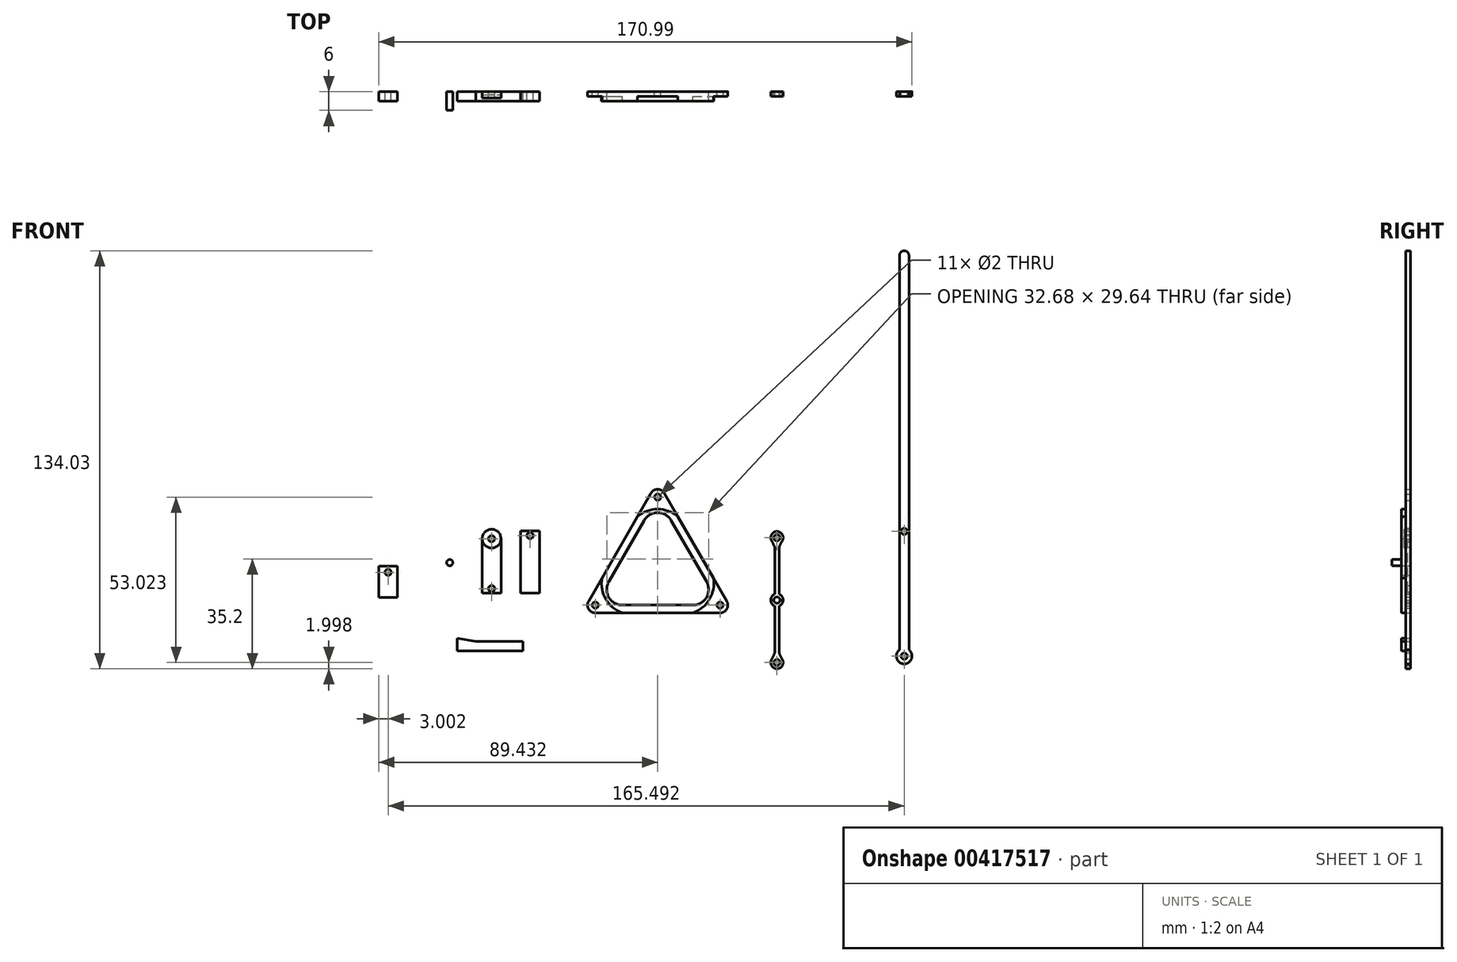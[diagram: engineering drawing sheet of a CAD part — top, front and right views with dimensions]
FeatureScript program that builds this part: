
annotation { "Feature Type Name" : "Feature", "Feature Type Description" : "" }
export const myFeature = defineFeature(function(context is Context, id is Id, definition is map)
    precondition{}
    {
        {
            var Q0;
            Q0=qCreatedBy(makeId("Front.planeOp"),FACE);
            var sketch = newSketch(context, id + "F0", { "sketchPlane" : qUnion([Q0])});
            skLineSegment(sketch, "E0.top", {"start": v(-62.3, 0) * mm, "end": v(-39.63, 0) * mm});
            skLineSegment(sketch, "E1", {"start": v(-55.3, 27.14) * mm, "end": v(-66.64, 7.5) * mm});
            skLineSegment(sketch, "E2", {"start": v(-46.64, 27.14) * mm, "end": v(-35.3, 7.5) * mm});
            skPoint(sketch, "E0.right.start.orphan", {"position": v(-30.97, 34.64) * mm});
            skPoint(sketch, "E0.bottom.start.orphan", {"position": v(-70.97, 34.64) * mm});
            skCircle(sketch, "E3", {"center": v(-50.97, 34.64) * mm, "radius": 2.5 * mm});
            skCircle(sketch, "E4", {"center": v(-70.97, 0) * mm, "radius": 2.5 * mm});
            skCircle(sketch, "E5", {"center": v(-30.97, 0) * mm, "radius": 2.5 * mm});
            skLineSegment(sketch, "E6", {"start": v(-70.97, -2.5) * mm, "end": v(-30.97, -2.5) * mm});
            skLineSegment(sketch, "E7", {"start": v(-28.8, 1.25) * mm, "end": v(-48.8, 35.9) * mm});
            skLineSegment(sketch, "E8", {"start": v(-53.13, 35.9) * mm, "end": v(-73.13, 1.25) * mm});
            skArc(sketch, "E9.filletArc", {"start": v(-66.64, 7.5) * mm, "mid": v(-66.64, 2.5) * mm, "end": v(-62.3, 0) * mm});
            skArc(sketch, "E10.filletArc", {"start": v(-39.63, 0) * mm, "mid": v(-35.3, 2.5) * mm, "end": v(-35.3, 7.5) * mm});
            skArc(sketch, "E11.filletArc", {"start": v(-46.64, 27.14) * mm, "mid": v(-50.97, 29.64) * mm, "end": v(-55.3, 27.14) * mm});
            skArc(sketch, "E12", {"start": v(-44.47, 28.4) * mm, "mid": v(-50.97, 30.79) * mm, "end": v(-57.46, 28.4) * mm});
            skArc(sketch, "E13", {"start": v(-68.8, 8.75) * mm, "mid": v(-67.63, 1.93) * mm, "end": v(-62.3, -2.5) * mm});
            skArc(sketch, "E14", {"start": v(-39.7, -2.5) * mm, "mid": v(-34.33, 1.9) * mm, "end": v(-33.13, 8.75) * mm});
            skCircle(sketch, "E15", {"center": v(-50.97, 34.64) * mm, "radius": 1 * mm});
            skCircle(sketch, "E16", {"center": v(-70.97, 0) * mm, "radius": 1 * mm});
            skCircle(sketch, "E17", {"center": v(-30.97, 0) * mm, "radius": 1 * mm});
            skSolve(sketch);
        }
        {
            var Q0;
            Q0=makeQuery(id+"F0.imprint","IMPRINT",FACE,{"disambiguationData":[TD([[makeQuery(id+"F0.imprint","IMPRINT",EDGE,{"derivedFrom":sQuery(id+"F0.wireOp",EDGE,"E0.top")}),-1.0]])]});
            extrude(context, id + "F1", {"entities" : qUnion([Q0]), "depth" : 3 * mm});
        }
        {
            var Q0;
            Q0=makeQuery(id+"F0.imprint","IMPRINT",FACE,{"disambiguationData":[TD([[makeQuery(id+"F0.imprint","IMPRINT",EDGE,{"derivedFrom":sQuery(id+"F0.wireOp",EDGE,"E15")}),-1.0]])]});
            var Q1;
            {var subQ5=sQuery(id+"F0.wireOp",EDGE,"E12");Q1=makeQuery(id+"F0.imprint","IMPRINT",FACE,{"disambiguationData":[TD([[makeQuery(id+"F0.imprint","IMPRINT",EDGE,{"derivedFrom":subQ5}),-1.0]])]});}
            var Q2;
            {var subQ5=sQuery(id+"F0.wireOp",EDGE,"E14");Q2=makeQuery(id+"F0.imprint","IMPRINT",FACE,{"disambiguationData":[TD([[makeQuery(id+"F0.imprint","IMPRINT",EDGE,{"derivedFrom":subQ5}),-1.0]])]});}
            var Q3;
            Q3=makeQuery(id+"F0.imprint","IMPRINT",FACE,{"disambiguationData":[TD([[makeQuery(id+"F0.imprint","IMPRINT",EDGE,{"derivedFrom":sQuery(id+"F0.wireOp",EDGE,"E17")}),-1.0]])]});
            var Q4;
            {var subQ5=sQuery(id+"F0.wireOp",EDGE,"E13");Q4=makeQuery(id+"F0.imprint","IMPRINT",FACE,{"disambiguationData":[TD([[makeQuery(id+"F0.imprint","IMPRINT",EDGE,{"derivedFrom":subQ5}),-1.0]])]});}
            var Q5;
            Q5=makeQuery(id+"F0.imprint","IMPRINT",FACE,{"disambiguationData":[TD([[makeQuery(id+"F0.imprint","IMPRINT",EDGE,{"derivedFrom":sQuery(id+"F0.wireOp",EDGE,"E16")}),-1.0]])]});
            extrude(context, id + "F2", {"entities" : qUnion([Q0, Q1, Q2, Q3, Q4, Q5]), "operationType" : NewBodyOperationType.ADD, "depth" : 1.5 * mm});
        }
        {
            var Q0;
            Q0=qCreatedBy(makeId("Front.planeOp"),FACE);
            var sketch = newSketch(context, id + "F3", { "sketchPlane" : qUnion([Q0])});
            skLineSegment(sketch, "E18.left", {"start": v(-13.46, 18.57) * mm, "end": v(-13.46, 3.48) * mm});
            skLineSegment(sketch, "E18.right", {"start": v(-12, 18.57) * mm, "end": v(-12, 3.48) * mm});
            skArc(sketch, "E19", {"start": v(-11.13, 20.41) * mm, "mid": v(-12.73, 23.62) * mm, "end": v(-14.32, 20.41) * mm});
            skCircle(sketch, "E20", {"center": v(-12.73, 21.62) * mm, "radius": 1 * mm});
            skLineSegment(sketch, "E21", {"start": v(-13.46, 18.57) * mm, "end": v(-12, 18.57) * mm});
            skArc(sketch, "E22", {"start": v(-13.46, 18.57) * mm, "mid": v(-13.84, 19.51) * mm, "end": v(-14.32, 20.41) * mm});
            skArc(sketch, "E23", {"start": v(-11.13, 20.41) * mm, "mid": v(-11.6, 19.51) * mm, "end": v(-12, 18.57) * mm});
            skPoint(sketch, "E24.trimOffspring.end.orphan", {"position": v(-12, 21.62) * mm});
            skPoint(sketch, "E18.bottom.start.orphan", {"position": v(-13.46, 21.62) * mm});
            skArc(sketch, "E25", {"start": v(-11.73, 1.62) * mm, "mid": v(-12.73, 2.62) * mm, "end": v(-13.73, 1.62) * mm});
            skArc(sketch, "E26.0", {"start": v(-10.73, 1.62) * mm, "mid": v(-11.07, 2.74) * mm, "end": v(-12, 3.48) * mm});
            skLineSegment(sketch, "E27", {"start": v(-13.73, 1.62) * mm, "end": v(-14.73, 1.62) * mm});
            skLineSegment(sketch, "E28", {"start": v(-11.73, 1.62) * mm, "end": v(-10.73, 1.62) * mm});
            skPoint(sketch, "E29.trimOffspring.end.orphan", {"position": v(-12, 1.62) * mm});
            skPoint(sketch, "E18.top.start.orphan", {"position": v(-13.46, 1.62) * mm});
            skArc(sketch, "E30.trimOffspring", {"start": v(-13.46, 3.48) * mm, "mid": v(-14.38, 2.74) * mm, "end": v(-14.73, 1.62) * mm});
            skSolve(sketch);
        }
        {
            var Q0;
            {var subQ0=sQuery(id+"F3.wireOp",EDGE,"E21");Q0=makeQuery(id+"F3.imprint","IMPRINT",FACE,{"disambiguationData":[TD([[makeQuery(id+"F3.imprint","IMPRINT",EDGE,{"derivedFrom":subQ0}),-1.0]])]});}
            extrude(context, id + "F4", {"entities" : qUnion([Q0]), "depth" : 1.5 * mm});
        }
        {
            var Q0;
            Q0=makeQuery(id+"F3.imprint","IMPRINT",FACE,{"disambiguationData":[TD([[makeQuery(id+"F3.imprint","IMPRINT",EDGE,{"derivedFrom":sQuery(id+"F3.wireOp",EDGE,"E19")}),1.0]])]});
            extrude(context, id + "F5", {"entities" : qUnion([Q0]), "operationType" : NewBodyOperationType.ADD, "depth" : 1.5 * mm});
        }
        {
            var Q0;
            Q0=makeQuery(id+"F4.opExtrude","SWEPT_BODY",BODY,{"disambiguationData":[OSD([sQuery(id+"F3.wireOp",EDGE,"E18.top"),sQuery(id+"F3.wireOp",EDGE,"E18.left"),sQuery(id+"F3.wireOp",EDGE,"E18.right"),sQuery(id+"F3.wireOp",EDGE,"E21")])]});
            var Q1;
            Q1=makeQuery(id+"F4.opExtrude","SWEPT_FACE",FACE,{"disambiguationData":[OSD([sQuery(id+"F3.wireOp",EDGE,"E27")])]});
            mirror(context, id + "F6", {"operationType" : NewBodyOperationType.ADD, "entities" : qUnion([Q0]), "mirrorPlane" : qUnion([Q1])});
        }
        {
            var Q0;
            Q0=qCreatedBy(makeId("Front.planeOp"),FACE);
            var sketch = newSketch(context, id + "F7", { "sketchPlane" : qUnion([Q0])});
            skCircle(sketch, "E31", {"center": v(-104.2, 21.3) * mm, "radius": 3 * mm});
            skLineSegment(sketch, "E32.bottom", {"start": v(-107.2, 21.3) * mm, "end": v(-101.2, 21.3) * mm});
            skLineSegment(sketch, "E32.top", {"start": v(-107.2, 3.8) * mm, "end": v(-101.2, 3.8) * mm});
            skLineSegment(sketch, "E32.left", {"start": v(-107.2, 21.3) * mm, "end": v(-107.2, 3.8) * mm});
            skLineSegment(sketch, "E32.right", {"start": v(-101.2, 21.3) * mm, "end": v(-101.2, 3.8) * mm});
            skCircle(sketch, "E33", {"center": v(-104.2, 5.3) * mm, "radius": 1 * mm});
            skCircle(sketch, "E34", {"center": v(-104.2, 21.3) * mm, "radius": 1 * mm});
            skLineSegment(sketch, "E35.bottom", {"start": v(-94.88, 23.8) * mm, "end": v(-88.88, 23.8) * mm});
            skLineSegment(sketch, "E35.top", {"start": v(-94.88, 3.8) * mm, "end": v(-88.88, 3.8) * mm});
            skLineSegment(sketch, "E35.left", {"start": v(-94.88, 23.8) * mm, "end": v(-94.88, 3.8) * mm});
            skLineSegment(sketch, "E35.right", {"start": v(-88.88, 23.8) * mm, "end": v(-88.88, 3.8) * mm});
            skLineSegment(sketch, "E36", {"start": v(-91.88, 23.8) * mm, "end": v(-91.88, 3.8) * mm, "construction": true});
            skCircle(sketch, "E37", {"center": v(-91.88, 22.3) * mm, "radius": 1 * mm});
            skCircle(sketch, "E38", {"center": v(-117.64, 13.63) * mm, "radius": 1 * mm});
            skLineSegment(sketch, "E39.bottom", {"start": v(-134.4, 2.52) * mm, "end": v(-140.4, 2.52) * mm});
            skLineSegment(sketch, "E39.top", {"start": v(-134.4, 12.52) * mm, "end": v(-140.4, 12.52) * mm});
            skLineSegment(sketch, "E39.left", {"start": v(-134.4, 2.52) * mm, "end": v(-134.4, 12.52) * mm});
            skLineSegment(sketch, "E39.right", {"start": v(-140.4, 2.52) * mm, "end": v(-140.4, 12.52) * mm});
            skPoint(sketch, "E39.middle", {"position": v(-137.4, 7.52) * mm});
            skCircle(sketch, "E40", {"center": v(-137.4, 10.52) * mm, "radius": 1 * mm});
            skPoint(sketch, "E40.centerSnap0", {"position": v(-137.4, 12.52) * mm});
            skSolve(sketch);
        }
        {
            var Q0;
            Q0=makeQuery(id+"F7.imprint","IMPRINT",FACE,{"disambiguationData":[TD([[makeQuery(id+"F7.imprint","IMPRINT",EDGE,{"derivedFrom":sQuery(id+"F7.wireOp",EDGE,"E35.bottom")}),-1.0]])]});
            var Q1;
            Q1=makeQuery(id+"F7.imprint","IMPRINT",FACE,{"disambiguationData":[TD([[makeQuery(id+"F7.imprint","IMPRINT",EDGE,{"derivedFrom":sQuery(id+"F7.wireOp",EDGE,"E35.top")}),-1.0]])]});
            extrude(context, id + "F8", {"entities" : qUnion([Q0, Q1]), "depth" : 3 * mm});
        }
        {
            var Q0;
            Q0=makeQuery(id+"F7.imprint","IMPRINT",FACE,{"disambiguationData":[TD([[makeQuery(id+"F7.imprint","IMPRINT",EDGE,{"derivedFrom":sQuery(id+"F7.wireOp",EDGE,"E38")}),1.0]])]});
            extrude(context, id + "F9", {"entities" : qUnion([Q0]), "depth" : 6 * mm});
        }
        {
            var Q0;
            {var subQ0=sQuery(id+"F7.wireOp",EDGE,"E32.bottom");var subQ4=sQuery(id+"F7.wireOp",EDGE,"E34");var subQ5=makeQuery(id+"F7.imprint","INTERSECT",VERTEX,{"disambiguationData":[OD(0.0)],"derivedFrom":[subQ0,subQ4]});Q0=makeQuery(id+"F7.imprint","IMPRINT",FACE,{"disambiguationData":[TD([[makeQuery(id+"F7.imprint","IMPRINT",EDGE,{"disambiguationData":[TD([[subQ5,-1.0]])],"derivedFrom":subQ4}),-1.0]])]});}
            var Q1;
            {var subQ0=sQuery(id+"F7.wireOp",EDGE,"E32.bottom");var subQ4=sQuery(id+"F7.wireOp",EDGE,"E34");var subQ5=makeQuery(id+"F7.imprint","INTERSECT",VERTEX,{"disambiguationData":[OD(0.0)],"derivedFrom":[subQ0,subQ4]});Q1=makeQuery(id+"F7.imprint","IMPRINT",FACE,{"disambiguationData":[TD([[makeQuery(id+"F7.imprint","IMPRINT",EDGE,{"disambiguationData":[TD([[subQ5,1.0]])],"derivedFrom":subQ4}),-1.0]])]});}
            extrude(context, id + "F10", {"entities" : qUnion([Q0, Q1]), "depth" : 2 * mm});
        }
        {
            var Q0;
            Q0=makeQuery(id+"F7.imprint","IMPRINT",FACE,{"disambiguationData":[TD([[makeQuery(id+"F7.imprint","IMPRINT",EDGE,{"derivedFrom":sQuery(id+"F7.wireOp",EDGE,"E32.top")}),1.0]])]});
            extrude(context, id + "F11", {"entities" : qUnion([Q0]), "operationType" : NewBodyOperationType.ADD, "depth" : 1 * mm});
        }
        {
            var Q0;
            Q0=qCreatedBy(makeId("Front.planeOp"),FACE);
            var sketch = newSketch(context, id + "F12", { "sketchPlane" : qUnion([Q0])});
            skLineSegment(sketch, "E41.bottom", {"start": v(29.6, -16.35) * mm, "end": v(26.6, -16.35) * mm});
            skLineSegment(sketch, "E41.top", {"start": v(28.1, 113.65) * mm, "end": v(28.1, 113.65) * mm});
            skLineSegment(sketch, "E41.left", {"start": v(29.6, -16.35) * mm, "end": v(29.6, 112.15) * mm});
            skLineSegment(sketch, "E41.right", {"start": v(26.6, -16.35) * mm, "end": v(26.6, 112.15) * mm});
            skPoint(sketch, "E41.middle", {"position": v(28.1, 48.65) * mm});
            skCircle(sketch, "E42", {"center": v(28.1, -16.35) * mm, "radius": 2.5 * mm});
            skCircle(sketch, "E43", {"center": v(28.1, -16.35) * mm, "radius": 1 * mm});
            skLineSegment(sketch, "E44", {"start": v(28.1, -16.35) * mm, "end": v(28.1, 23.65) * mm, "construction": true});
            skCircle(sketch, "E45", {"center": v(28.1, 23.65) * mm, "radius": 1 * mm});
            skPoint(sketch, "E46.visualSharp", {"position": v(26.6, 113.65) * mm});
            skArc(sketch, "E46.filletArc", {"start": v(28.1, 113.65) * mm, "mid": v(27.03, 113.22) * mm, "end": v(26.6, 112.15) * mm});
            skPoint(sketch, "E47.visualSharp", {"position": v(29.6, 113.65) * mm});
            skArc(sketch, "E47.filletArc", {"start": v(29.6, 112.15) * mm, "mid": v(29.15, 113.22) * mm, "end": v(28.1, 113.65) * mm});
            skSolve(sketch);
        }
        {
            var Q0;
            Q0=makeQuery(id+"F12.imprint","IMPRINT",FACE,{"disambiguationData":[TD([[makeQuery(id+"F12.imprint","IMPRINT",EDGE,{"derivedFrom":sQuery(id+"F12.wireOp",EDGE,"E45")}),-1.0]])]});
            var Q1;
            {var subQ0=sQuery(id+"F12.wireOp",EDGE,"E41.left");var subQ1=sQuery(id+"F12.wireOp",EDGE,"E41.bottom");var subQ2=makeQuery(id+"F12.imprint","INTERSECT",VERTEX,{"derivedFrom":[subQ1,subQ0]});Q1=makeQuery(id+"F12.imprint","IMPRINT",FACE,{"disambiguationData":[TD([[makeQuery(id+"F12.imprint","IMPRINT",EDGE,{"disambiguationData":[TD([[subQ2,-1.0]])],"derivedFrom":subQ1}),1.0]])]});}
            var Q2;
            {var subQ0=sQuery(id+"F12.wireOp",EDGE,"E41.left");var subQ1=sQuery(id+"F12.wireOp",EDGE,"E41.bottom");var subQ2=makeQuery(id+"F12.imprint","INTERSECT",VERTEX,{"derivedFrom":[subQ1,subQ0]});Q2=makeQuery(id+"F12.imprint","IMPRINT",FACE,{"disambiguationData":[TD([[makeQuery(id+"F12.imprint","IMPRINT",EDGE,{"disambiguationData":[TD([[subQ2,-1.0]])],"derivedFrom":subQ1}),-1.0]])]});}
            extrude(context, id + "F13", {"entities" : qUnion([Q0, Q1, Q2]), "depth" : 1.5 * mm});
        }
        {
            var Q0;
            Q0=makeQuery(id+"F7.imprint","IMPRINT",FACE,{"disambiguationData":[TD([[makeQuery(id+"F7.imprint","IMPRINT",EDGE,{"derivedFrom":sQuery(id+"F7.wireOp",EDGE,"E39.bottom")}),-1.0]])]});
            extrude(context, id + "F14", {"entities" : qUnion([Q0]), "depth" : 3 * mm});
        }
        {
            var Q0;
            Q0=qCreatedBy(makeId("Front.planeOp"),FACE);
            var sketch = newSketch(context, id + "F15", { "sketchPlane" : qUnion([Q0])});
            skLineSegment(sketch, "E48.bottom", {"start": v(-109.33, -11.62) * mm, "end": v(-94.2, -11.62) * mm});
            skLineSegment(sketch, "E48.top", {"start": v(-115.23, -14.62) * mm, "end": v(-94.2, -14.62) * mm});
            skLineSegment(sketch, "E48.right", {"start": v(-94.2, -11.62) * mm, "end": v(-94.2, -14.62) * mm});
            skLineSegment(sketch, "E49.top", {"start": v(-115.23, -14.62) * mm, "end": v(-109.23, -14.62) * mm});
            skPoint(sketch, "E48.left.start.orphan", {"position": v(-113.08, -11.62) * mm});
            skLineSegment(sketch, "E50", {"start": v(-115.23, -10.58) * mm, "end": v(-109.33, -11.62) * mm});
            skLineSegment(sketch, "E51", {"start": v(-115.23, -10.58) * mm, "end": v(-115.23, -14.62) * mm});
            skPoint(sketch, "E52.orphan", {"position": v(-111.2, -11.62) * mm});
            skSolve(sketch);
        }
        {
            var Q0;
            Q0=makeQuery(id+"F15.imprint","IMPRINT",FACE,{"disambiguationData":[TD([[makeQuery(id+"F15.imprint","IMPRINT",EDGE,{"derivedFrom":sQuery(id+"F15.wireOp",EDGE,"E48.bottom")}),-1.0]])]});
            extrude(context, id + "F16", {"entities" : qUnion([Q0]), "depth" : 3 * mm});
        }
    });
